# Revit family: Gorter BV-FL THERMO 500x500mm
name_source: partatom
category: Generic Models
units: mm (PartAtom-declared; Revit-internal decimal feet)

## family parameters
Can host rebar = No
Cut with Voids When Loaded = Yes
Host = Face
Part Type = Normal
Room Calculation Point = No
Round Connector Dimension = Use Diameter
Shared = Yes

## types (5) — shared parameters
Manufacturer = Gorter
Model = BV-FL THERMO
belasting = 15 kN
binnenluik = tbv betonvulling
brandwerend 90 min = nee
gasdrukveer = nee
geïsoleerd = ja
materiaal = bcb_staal
rubberen_afdichting = enkel
scharnierend = nee
sluiting hoek = Yes
sluiting y-as = Yes
vergrendeling = nee
vullen_met_beton = ja
zero-valued in all types: Default Elevation

## per-type parameters (varying)
| type | Description | binnenmaat_breedte | binnenmaat_lengte | gewicht | sluiting | sluiting x-as | uitwendige_breedte | uitwendige_lengte |
| BV-FL THERMO 600x600mm | BV-FL THERMO 66 | 600 mm  [stored 1.9685 ft] | 600 mm  [stored 1.9685 ft] | 23 | 4 | Yes | 730 mm  [stored 2.39501 ft] | 730 mm  [stored 2.39501 ft] |
| BV-FL THERMO 800x600mm | BV-FL THERMO 86 | 600 mm  [stored 1.9685 ft] | 800 mm  [stored 2.62467 ft] | 29 | 6 | No | 730 mm  [stored 2.39501 ft] | 930 mm  [stored 3.05118 ft] |
| BV-FL THERMO 800x800mm | BV-FL THERMO 88 | 800 mm  [stored 2.62467 ft] | 800 mm  [stored 2.62467 ft] | 33 | 8 | Yes | 930 mm  [stored 3.05118 ft] | 930 mm  [stored 3.05118 ft] |
| BV-FL THERMO 1000x600mm | BV-FL THERMO 106 | 1000 mm  [stored 3.28084 ft] | 600 mm  [stored 1.9685 ft] | 33 | 6 | No | 1130 mm  [stored 3.70735 ft] | 730 mm  [stored 2.39501 ft] |
| BV-FL THERMO 500x500mm | BV-FL THERMO 55 | 500 mm  [stored 1.64042 ft] | 500 mm  [stored 1.64042 ft] | 23 | 4 | Yes | 630 mm  [stored 2.06693 ft] | 630 mm  [stored 2.06693 ft] |

note: [stored X ft] marks values corroborated as IEEE doubles in the binary element streams (Revit-internal decimal feet)

## geometry (parser evidence)
native form markers: Blend x2, Sweep x7
no freeform markers — native parametric forms only
